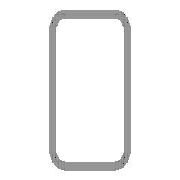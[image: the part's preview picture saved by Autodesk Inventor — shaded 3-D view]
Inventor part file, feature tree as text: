
AUTODESK INVENTOR PART (.ipt)
format: ipt  version: 2025.3 (Build 293356000, 356)  size: 148,992 bytes
history: native  units: mm (DEFAULTED — no unit token found)
features: other x4, plane x3, split x2, sketch x1
ambient origin geometry x8: Origin, YZ Plane, XZ Plane, XY Plane, X Axis, Y Axis, Z Axis, Center Point
bodies: Solid1 (feature_tree), Body (feature_tree)
feature tree (10):
  parser-record x1  (decoder bookkeeping rows leaked as tree rows — omitted from the tree; the rows remain in map.json)
  other  "Driven Length"
  other  "Start Plane"
  other  "End Plane"
  plane  "Work Plane4"
  split  "Split1"
  plane  "Work Plane5"
  split  "Split2"
  sketch  "Sketch3"  dims[d3=2924.995667mm d4=0.0mm d7=4.0mm d9=20.0mm d11=40.0mm d12=2.0mm d13=73.137085mm d14=2998.132752mm d15=10.0mm d16=20.0mm d17=90.0deg d18=2924.995667mm]
  plane  "Work Plane3"
